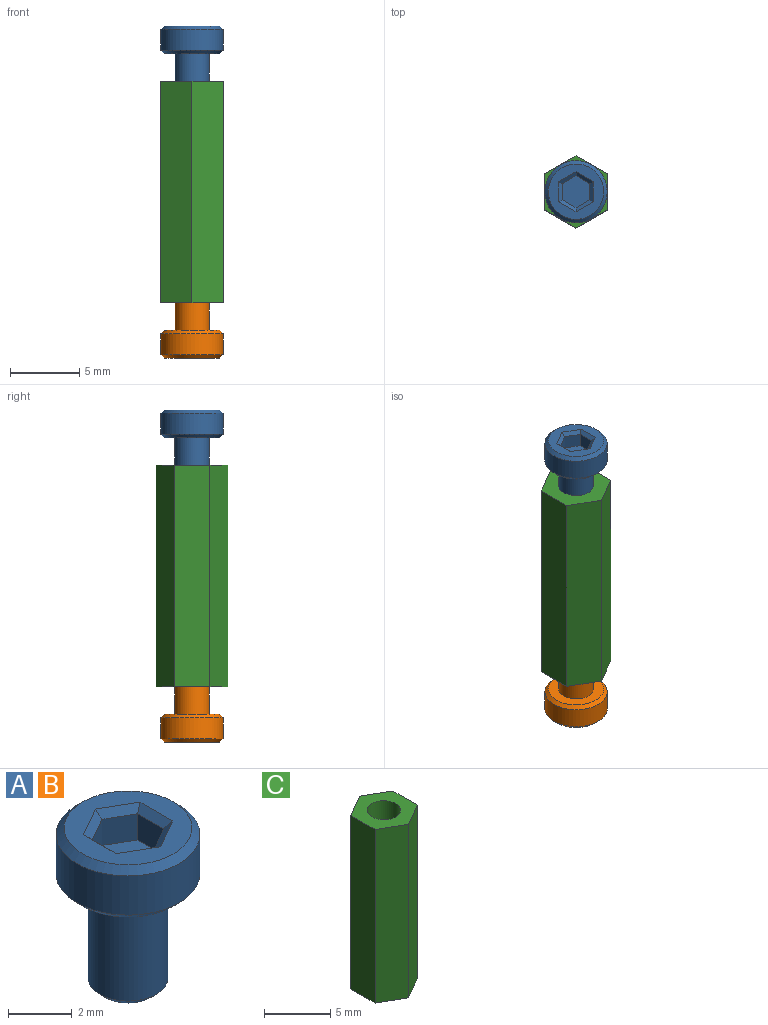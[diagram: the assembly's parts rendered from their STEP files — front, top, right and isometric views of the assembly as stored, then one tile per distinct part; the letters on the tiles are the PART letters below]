
ASSEMBLY  parts=3 mates=2
PART A: 21 faces, bbox 4.5x4.5x6 mm
  f0: plane 4x4mm, normal (0,0,1), area 7.2mm2, adj f12,f13,f14,f15,f16,f17,f18
  f1: cylinder r=1.25mm len=3.75mm, axis (0,0,1), area 29.5mm2, adj f4,f20
  f2: plane 2x2mm, normal (0,0,-1), area 3.1mm2, adj f20
  f3: cylinder r=2.25mm len=4.5mm, axis (0,0,-1), area 21.2mm2, adj f18,f19
  f4: plane 4x4mm, normal (0,0,-1), area 7.7mm2, adj f1,f19
  f5: plane 1x1mm, normal (-0.5,0.87,0), area 1.2mm2, adj f6,f10,f11,f17
  f6: plane 1.15x1mm, normal (-1,0,0), area 1.2mm2, adj f5,f7,f11,f15
  f7: plane 1x1mm, normal (-0.5,-0.87,0), area 1.2mm2, adj f6,f8,f11,f13
  f8: plane 1x1mm, normal (0.5,-0.87,0), area 1.2mm2, adj f7,f9,f11,f12
  f9: plane 1.15x1mm, normal (1,0,0), area 1.2mm2, adj f8,f10,f11,f14
  f10: plane 1x1mm, normal (0.5,0.87,0), area 1.2mm2, adj f5,f9,f11,f16
  f11: plane 2.31x2mm, normal (0,0,1), area 3.5mm2, adj f5,f6,f7,f8,f9,f10
  f12: plane 1.25x0.87mm, normal (0.35,-0.61,0.71), area 0.5mm2, adj f0,f8,f13,f14
  f13: plane 1.25x0.87mm, normal (-0.35,-0.61,0.71), area 0.5mm2, adj f0,f7,f12,f15
  f14: plane 1.44x0.25mm, normal (0.71,0,0.71), area 0.5mm2, adj f0,f9,f12,f16
  f15: plane 1.44x0.25mm, normal (-0.71,0,0.71), area 0.5mm2, adj f0,f6,f13,f17
  f16: plane 1.25x0.87mm, normal (0.35,0.61,0.71), area 0.5mm2, adj f0,f10,f14,f17
  f17: plane 1.25x0.87mm, normal (-0.35,0.61,0.71), area 0.5mm2, adj f0,f5,f15,f16
  f18: cone r=2mm half-angle=45deg, axis (0,0,-1), area 4.7mm2, adj f0,f3
  f19: cone r=2.25mm half-angle=45deg, axis (0,0,1), area 4.7mm2, adj f3,f4
  f20: cone r=1.25mm half-angle=45deg, axis (0,0,1), area 2.5mm2, adj f1,f2
PART B: same geometry as A
PART C: 9 faces, bbox 4.5x5.2x16 mm
  f0: plane 16x2.6mm, normal (1,0,0), area 41.6mm2, adj f1,f6,f7,f8
  f1: plane 16x2.25mm, normal (0.5,0.87,0), area 41.6mm2, adj f0,f2,f7,f8
  f2: plane 16x2.25mm, normal (-0.5,0.87,0), area 41.6mm2, adj f1,f3,f7,f8
  f3: plane 16x2.6mm, normal (-1,0,0), area 41.6mm2, adj f2,f4,f7,f8
  f4: plane 16x2.25mm, normal (-0.5,-0.87,0), area 41.6mm2, adj f3,f6,f7,f8
  f5: cylinder r=1.25mm len=16mm, axis (0,0,1), area 125.7mm2, adj f7,f8
  f6: plane 16x2.25mm, normal (0.5,-0.87,0), area 41.6mm2, adj f0,f4,f7,f8
  f7: plane 5.2x4.5mm, normal (0,0,-1), area 12.6mm2, adj f0,f1,f2,f3,f4,f5,f6
  f8: plane 5.2x4.5mm, normal (0,0,1), area 12.6mm2, adj f0,f1,f2,f3,f4,f5,f6
PLACE A t=(-8.82,0,-7.45)mm
PLACE B rot(axis=(1,0,0),180deg) t=(-8.82,0,-27.45)mm
PLACE C t=(-8.82,0,-9.45)mm
MATE fastened C.f5 <-> A.f1  axis (0,0,1) through (-8.82,0,-9.45)mm
MATE fastened B.f1 <-> C.f5  axis (0,0,1) through (-8.82,0,-27.45)mm
